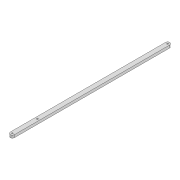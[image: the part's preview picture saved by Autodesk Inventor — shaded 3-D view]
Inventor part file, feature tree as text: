
AUTODESK INVENTOR PART (.ipt)
format: ipt  version: 2022 (Build 260153000, 153)  size: 92,672 bytes
history: native  units: mm
features: extrude x1, sketch x1
ambient origin geometry x8: Origin, YZ Plane, XZ Plane, XY Plane, X Axis, Y Axis, Z Axis, Center Point
bodies: Solid1 (feature_tree)
feature tree (2):
  extrude  "Extrusion1"  Depth=57.376mm
  sketch  "Sketch1"  dims[d0=3.3mm d1=3.3mm d2=10.0mm d3=355.998mm d6=6.0mm d7=0.0mm d14=3.3mm d15=57.376mm]
